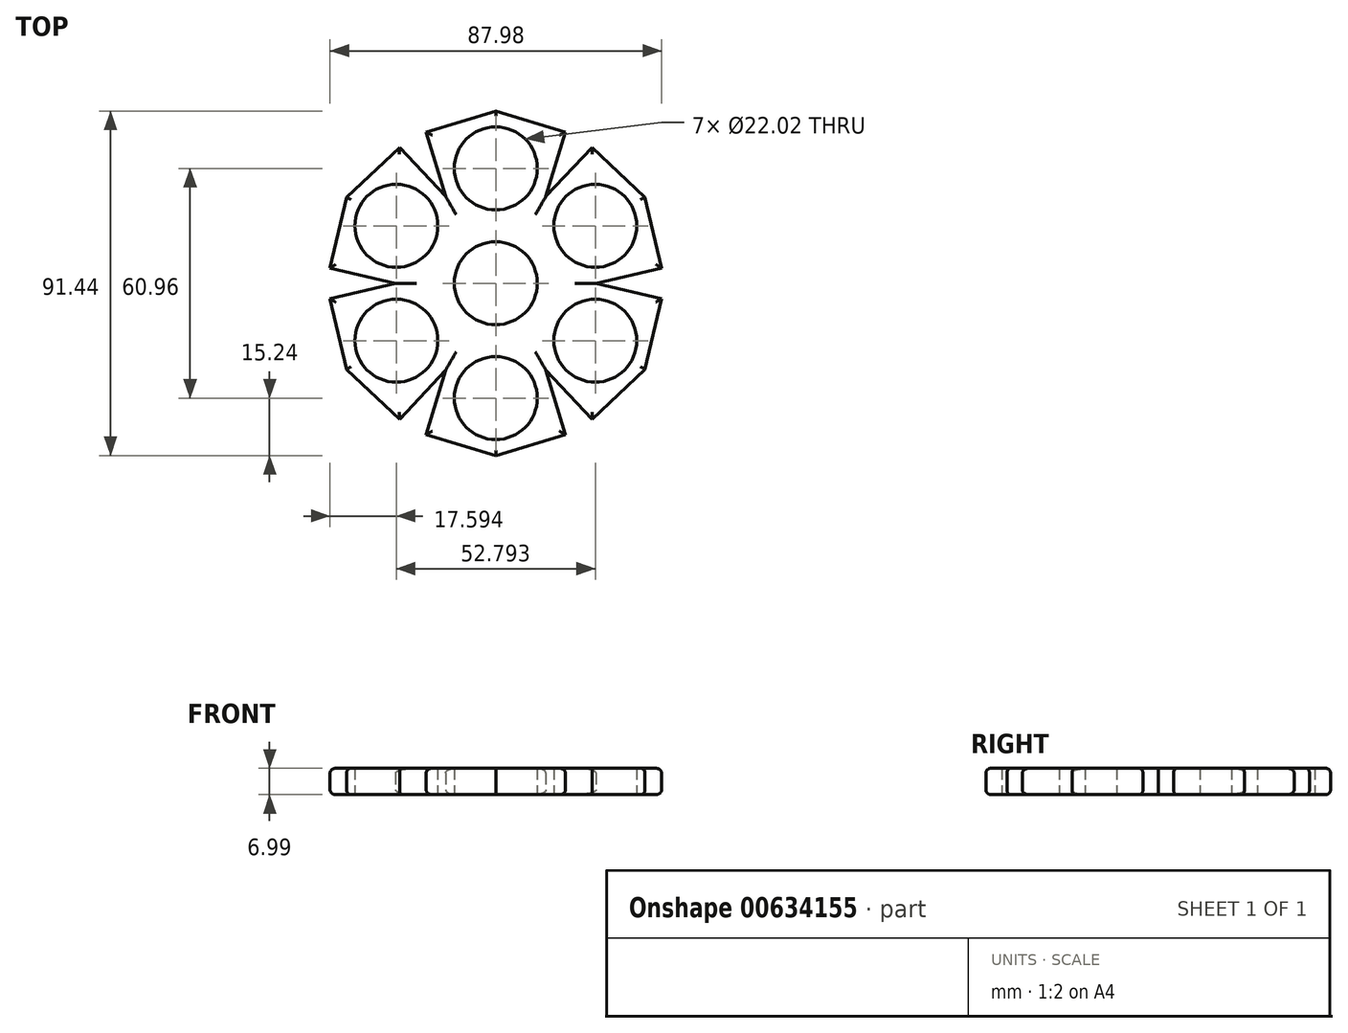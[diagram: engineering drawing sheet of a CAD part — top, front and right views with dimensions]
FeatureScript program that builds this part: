
annotation { "Feature Type Name" : "Feature", "Feature Type Description" : "" }
export const myFeature = defineFeature(function(context is Context, id is Id, definition is map)
    precondition{}
    {
        {
            var Q0;
            Q0=qCreatedBy(makeId("Top.planeOp"),FACE);
            var sketch = newSketch(context, id + "F0", { "sketchPlane" : qUnion([Q0])});
            skCircle(sketch, "E0", {"center": v(0, 0) * mm, "radius": 11.01 * mm});
            skLineSegment(sketch, "E1", {"start": v(0, 0) * mm, "end": v(0, 30.48) * mm});
            skCircle(sketch, "E2", {"center": v(0, 30.48) * mm, "radius": 11.01 * mm});
            skCircle(sketch, "E3", {"center": v(0, 0) * mm, "radius": 14.23 * mm});
            skLineSegment(sketch, "E4", {"start": v(-9.52, 10.57) * mm, "end": v(-18.48, 40.12) * mm});
            skLineSegment(sketch, "E5", {"start": v(-18.48, 40.12) * mm, "end": v(0, 45.72) * mm});
            skLineSegment(sketch, "E6", {"start": v(0, 45.72) * mm, "end": v(18.48, 40.12) * mm});
            skLineSegment(sketch, "E7", {"start": v(18.48, 40.12) * mm, "end": v(9.52, 10.57) * mm});
            skLineSegment(sketch, "E8", {"start": v(0, 45.72) * mm, "end": v(0, 0) * mm});
            skLineSegment(sketch, "E9.1.0", {"start": v(-39.6, 22.86) * mm, "end": v(0, 0) * mm});
            skCircle(sketch, "E9.1.1", {"center": v(-26.4, 15.24) * mm, "radius": 11.01 * mm});
            skLineSegment(sketch, "E9.1.2", {"start": v(-25.51, 36.06) * mm, "end": v(-4.4, 13.53) * mm});
            skLineSegment(sketch, "E9.1.3", {"start": v(-39.6, 22.86) * mm, "end": v(-25.51, 36.06) * mm});
            skLineSegment(sketch, "E9.1.4", {"start": v(-43.99, 4.06) * mm, "end": v(-39.6, 22.86) * mm});
            skLineSegment(sketch, "E9.1.5", {"start": v(-13.92, -2.96) * mm, "end": v(-43.99, 4.06) * mm});
            skLineSegment(sketch, "E9.2.0", {"start": v(-39.6, -22.86) * mm, "end": v(0, 0) * mm});
            skCircle(sketch, "E9.2.1", {"center": v(-26.4, -15.24) * mm, "radius": 11.01 * mm});
            skLineSegment(sketch, "E9.2.2", {"start": v(-43.99, -4.06) * mm, "end": v(-13.92, 2.96) * mm});
            skLineSegment(sketch, "E9.2.3", {"start": v(-39.6, -22.86) * mm, "end": v(-43.99, -4.06) * mm});
            skLineSegment(sketch, "E9.2.4", {"start": v(-25.51, -36.06) * mm, "end": v(-39.6, -22.86) * mm});
            skLineSegment(sketch, "E9.2.5", {"start": v(-4.4, -13.53) * mm, "end": v(-25.51, -36.06) * mm});
            skLineSegment(sketch, "E9.3.0", {"start": v(0, -45.72) * mm, "end": v(0, 0) * mm});
            skCircle(sketch, "E9.3.1", {"center": v(0, -30.48) * mm, "radius": 11.01 * mm});
            skLineSegment(sketch, "E9.3.2", {"start": v(-18.48, -40.12) * mm, "end": v(-9.53, -10.57) * mm});
            skLineSegment(sketch, "E9.3.3", {"start": v(0, -45.72) * mm, "end": v(-18.48, -40.12) * mm});
            skLineSegment(sketch, "E9.3.4", {"start": v(18.48, -40.12) * mm, "end": v(0, -45.72) * mm});
            skLineSegment(sketch, "E9.3.5", {"start": v(9.52, -10.57) * mm, "end": v(18.48, -40.12) * mm});
            skLineSegment(sketch, "E9.4.0", {"start": v(39.6, -22.86) * mm, "end": v(0, 0) * mm});
            skCircle(sketch, "E9.4.1", {"center": v(26.4, -15.24) * mm, "radius": 11.01 * mm});
            skLineSegment(sketch, "E9.4.2", {"start": v(25.51, -36.06) * mm, "end": v(4.4, -13.53) * mm});
            skLineSegment(sketch, "E9.4.3", {"start": v(39.6, -22.86) * mm, "end": v(25.51, -36.06) * mm});
            skLineSegment(sketch, "E9.4.4", {"start": v(43.99, -4.06) * mm, "end": v(39.6, -22.86) * mm});
            skLineSegment(sketch, "E9.4.5", {"start": v(13.92, 2.96) * mm, "end": v(43.99, -4.06) * mm});
            skLineSegment(sketch, "E9.5.0", {"start": v(39.6, 22.86) * mm, "end": v(0, 0) * mm});
            skCircle(sketch, "E9.5.1", {"center": v(26.4, 15.24) * mm, "radius": 11.01 * mm});
            skLineSegment(sketch, "E9.5.2", {"start": v(43.99, 4.06) * mm, "end": v(13.92, -2.96) * mm});
            skLineSegment(sketch, "E9.5.3", {"start": v(39.6, 22.86) * mm, "end": v(43.99, 4.06) * mm});
            skLineSegment(sketch, "E9.5.4", {"start": v(25.51, 36.06) * mm, "end": v(39.6, 22.86) * mm});
            skLineSegment(sketch, "E9.5.5", {"start": v(4.4, 13.53) * mm, "end": v(25.51, 36.06) * mm});
            skSolve(sketch);
        }
        {
            var Q0;
            Q0 = qSketchRegion(id + "F0", true);
            var Q1;
            {var subQ3=sQuery(id+"F0.wireOp",EDGE,"E9.1.0");var subQ7=sQuery(id+"F0.wireOp",EDGE,"E0");var subQ8=makeQuery(id+"F0.imprint","INTERSECT",VERTEX,{"derivedFrom":[subQ7,subQ3]});Q1=makeQuery(id+"F0.imprint","IMPRINT",FACE,{"disambiguationData":[TD([[makeQuery(id+"F0.imprint","IMPRINT",EDGE,{"disambiguationData":[TD([[subQ8,-1.0]])],"derivedFrom":subQ7}),-1.0]])]});}
            var Q2;
            {var subQ4=sQuery(id+"F0.wireOp",EDGE,"E8");var subQ5=sQuery(id+"F0.wireOp",EDGE,"E0");var subQ6=makeQuery(id+"F0.imprint","INTERSECT",VERTEX,{"derivedFrom":[subQ5,subQ4]});Q2=makeQuery(id+"F0.imprint","IMPRINT",FACE,{"disambiguationData":[TD([[makeQuery(id+"F0.imprint","IMPRINT",EDGE,{"disambiguationData":[TD([[subQ6,-1.0]])],"derivedFrom":subQ5}),-1.0]])]});}
            var Q3;
            {var subQ2=sQuery(id+"F0.wireOp",EDGE,"E8");var subQ4=sQuery(id+"F0.wireOp",EDGE,"E0");var subQ5=makeQuery(id+"F0.imprint","INTERSECT",VERTEX,{"derivedFrom":[subQ4,subQ2]});Q3=makeQuery(id+"F0.imprint","IMPRINT",FACE,{"disambiguationData":[TD([[makeQuery(id+"F0.imprint","IMPRINT",EDGE,{"disambiguationData":[TD([[subQ5,1.0]])],"derivedFrom":subQ4}),-1.0]])]});}
            var Q4;
            {var subQ5=sQuery(id+"F0.wireOp",EDGE,"E9.5.0");var subQ7=sQuery(id+"F0.wireOp",EDGE,"E0");var subQ9=makeQuery(id+"F0.imprint","INTERSECT",VERTEX,{"derivedFrom":[subQ7,subQ5]});Q4=makeQuery(id+"F0.imprint","IMPRINT",FACE,{"disambiguationData":[TD([[makeQuery(id+"F0.imprint","IMPRINT",EDGE,{"disambiguationData":[TD([[subQ9,1.0]])],"derivedFrom":subQ7}),-1.0]])]});}
            var Q5;
            {var subQ4=sQuery(id+"F0.wireOp",EDGE,"E9.3.0");var subQ5=sQuery(id+"F0.wireOp",EDGE,"E0");var subQ6=makeQuery(id+"F0.imprint","INTERSECT",VERTEX,{"derivedFrom":[subQ5,subQ4]});Q5=makeQuery(id+"F0.imprint","IMPRINT",FACE,{"disambiguationData":[TD([[makeQuery(id+"F0.imprint","IMPRINT",EDGE,{"disambiguationData":[TD([[subQ6,-1.0]])],"derivedFrom":subQ5}),-1.0]])]});}
            var Q6;
            {var subQ5=sQuery(id+"F0.wireOp",EDGE,"E9.2.0");var subQ7=sQuery(id+"F0.wireOp",EDGE,"E0");var subQ8=makeQuery(id+"F0.imprint","INTERSECT",VERTEX,{"derivedFrom":[subQ7,subQ5]});Q6=makeQuery(id+"F0.imprint","IMPRINT",FACE,{"disambiguationData":[TD([[makeQuery(id+"F0.imprint","IMPRINT",EDGE,{"disambiguationData":[TD([[subQ8,-1.0]])],"derivedFrom":subQ7}),-1.0]])]});}
            extrude(context, id + "F1", {"entities" : qUnion([Q0, Q1, Q2, Q3, Q4, Q5, Q6]), "depth" : 7 * mm, "offsetDistance" : 25.4 * mm});
        }
        {
            var Q0;
            Q0=makeQuery(id+"F1.opExtrude","CAP_EDGE",EDGE,{"disambiguationData":[OSD([sQuery(id+"F0.wireOp",EDGE,"E6")])],"isStart":false});
            var Q1;
            Q1=makeQuery(id+"F1.opExtrude","CAP_EDGE",EDGE,{"disambiguationData":[OSD([sQuery(id+"F0.wireOp",EDGE,"E7")])],"isStart":false});
            var Q2;
            Q2=makeQuery(id+"F1.opExtrude","CAP_EDGE",EDGE,{"disambiguationData":[OSD([sQuery(id+"F0.wireOp",EDGE,"E9.5.5")])],"isStart":false});
            var Q3;
            Q3=makeQuery(id+"F1.opExtrude","CAP_EDGE",EDGE,{"disambiguationData":[OSD([sQuery(id+"F0.wireOp",EDGE,"E9.5.4")])],"isStart":false});
            var Q4;
            Q4=makeQuery(id+"F1.opExtrude","CAP_EDGE",EDGE,{"disambiguationData":[OSD([sQuery(id+"F0.wireOp",EDGE,"E9.5.3")])],"isStart":false});
            var Q5;
            Q5=makeQuery(id+"F1.opExtrude","CAP_EDGE",EDGE,{"disambiguationData":[OSD([sQuery(id+"F0.wireOp",EDGE,"E9.5.2")])],"isStart":false});
            var Q6;
            Q6=makeQuery(id+"F1.opExtrude","CAP_EDGE",EDGE,{"disambiguationData":[OSD([sQuery(id+"F0.wireOp",EDGE,"E9.4.5")])],"isStart":false});
            var Q7;
            Q7=makeQuery(id+"F1.opExtrude","CAP_EDGE",EDGE,{"disambiguationData":[OSD([sQuery(id+"F0.wireOp",EDGE,"E9.4.2")])],"isStart":false});
            var Q8;
            Q8=makeQuery(id+"F1.opExtrude","CAP_EDGE",EDGE,{"disambiguationData":[OSD([sQuery(id+"F0.wireOp",EDGE,"E9.3.5")])],"isStart":false});
            var Q9;
            Q9=makeQuery(id+"F1.opExtrude","CAP_EDGE",EDGE,{"disambiguationData":[OSD([sQuery(id+"F0.wireOp",EDGE,"E9.3.2")])],"isStart":false});
            var Q10;
            Q10=makeQuery(id+"F1.opExtrude","CAP_EDGE",EDGE,{"disambiguationData":[OSD([sQuery(id+"F0.wireOp",EDGE,"E9.2.5")])],"isStart":false});
            var Q11;
            Q11=makeQuery(id+"F1.opExtrude","CAP_EDGE",EDGE,{"disambiguationData":[OSD([sQuery(id+"F0.wireOp",EDGE,"E9.2.2")])],"isStart":false});
            var Q12;
            Q12=makeQuery(id+"F1.opExtrude","CAP_EDGE",EDGE,{"disambiguationData":[OSD([sQuery(id+"F0.wireOp",EDGE,"E9.1.5")])],"isStart":false});
            var Q13;
            Q13=makeQuery(id+"F1.opExtrude","CAP_EDGE",EDGE,{"disambiguationData":[OSD([sQuery(id+"F0.wireOp",EDGE,"E9.1.2")])],"isStart":false});
            var Q14;
            Q14=makeQuery(id+"F1.opExtrude","CAP_EDGE",EDGE,{"disambiguationData":[OSD([sQuery(id+"F0.wireOp",EDGE,"E4")])],"isStart":false});
            var Q15;
            Q15=makeQuery(id+"F1.opExtrude","CAP_EDGE",EDGE,{"disambiguationData":[OSD([sQuery(id+"F0.wireOp",EDGE,"E5")])],"isStart":false});
            var Q16;
            Q16=makeQuery(id+"F1.opExtrude","CAP_EDGE",EDGE,{"disambiguationData":[OSD([sQuery(id+"F0.wireOp",EDGE,"E9.1.3")])],"isStart":false});
            var Q17;
            Q17=makeQuery(id+"F1.opExtrude","CAP_EDGE",EDGE,{"disambiguationData":[OSD([sQuery(id+"F0.wireOp",EDGE,"E9.1.4")])],"isStart":false});
            var Q18;
            Q18=makeQuery(id+"F1.opExtrude","CAP_EDGE",EDGE,{"disambiguationData":[OSD([sQuery(id+"F0.wireOp",EDGE,"E9.2.3")])],"isStart":false});
            var Q19;
            Q19=makeQuery(id+"F1.opExtrude","CAP_EDGE",EDGE,{"disambiguationData":[OSD([sQuery(id+"F0.wireOp",EDGE,"E9.2.4")])],"isStart":false});
            var Q20;
            Q20=makeQuery(id+"F1.opExtrude","CAP_EDGE",EDGE,{"disambiguationData":[OSD([sQuery(id+"F0.wireOp",EDGE,"E9.3.3")])],"isStart":false});
            var Q21;
            Q21=makeQuery(id+"F1.opExtrude","CAP_EDGE",EDGE,{"disambiguationData":[OSD([sQuery(id+"F0.wireOp",EDGE,"E9.3.4")])],"isStart":false});
            var Q22;
            Q22=makeQuery(id+"F1.opExtrude","CAP_EDGE",EDGE,{"disambiguationData":[OSD([sQuery(id+"F0.wireOp",EDGE,"E9.4.3")])],"isStart":false});
            var Q23;
            Q23=makeQuery(id+"F1.opExtrude","CAP_EDGE",EDGE,{"disambiguationData":[OSD([sQuery(id+"F0.wireOp",EDGE,"E9.4.4")])],"isStart":false});
            fillet(context, id + "F2", {"entities" : qUnion([Q0, Q1, Q2, Q3, Q4, Q5, Q6, Q7, Q8, Q9, Q10, Q11, Q12, Q13, Q14, Q15, Q16, Q17, Q18, Q19, Q20, Q21, Q22, Q23]), "radius" : 1.27 * mm, "tangentPropagation" : true, "allowEdgeOverflow" : false});
        }
        {
            var Q0;
            Q0=makeQuery(id+"F1.opExtrude","CAP_EDGE",EDGE,{"disambiguationData":[OSD([sQuery(id+"F0.wireOp",EDGE,"E9.2.4")])],"isStart":true});
            var Q1;
            Q1=makeQuery(id+"F1.opExtrude","CAP_EDGE",EDGE,{"disambiguationData":[OSD([sQuery(id+"F0.wireOp",EDGE,"E9.2.3")])],"isStart":true});
            var Q2;
            Q2=makeQuery(id+"F1.opExtrude","CAP_EDGE",EDGE,{"disambiguationData":[OSD([sQuery(id+"F0.wireOp",EDGE,"E9.2.2")])],"isStart":true});
            var Q3;
            Q3=makeQuery(id+"F1.opExtrude","CAP_EDGE",EDGE,{"disambiguationData":[OSD([sQuery(id+"F0.wireOp",EDGE,"E9.1.5")])],"isStart":true});
            var Q4;
            Q4=makeQuery(id+"F1.opExtrude","CAP_EDGE",EDGE,{"disambiguationData":[OSD([sQuery(id+"F0.wireOp",EDGE,"E9.1.4")])],"isStart":true});
            var Q5;
            Q5=makeQuery(id+"F1.opExtrude","CAP_EDGE",EDGE,{"disambiguationData":[OSD([sQuery(id+"F0.wireOp",EDGE,"E9.1.3")])],"isStart":true});
            var Q6;
            Q6=makeQuery(id+"F1.opExtrude","CAP_EDGE",EDGE,{"disambiguationData":[OSD([sQuery(id+"F0.wireOp",EDGE,"E9.1.2")])],"isStart":true});
            var Q7;
            Q7=makeQuery(id+"F1.opExtrude","CAP_EDGE",EDGE,{"disambiguationData":[OSD([sQuery(id+"F0.wireOp",EDGE,"E4")])],"isStart":true});
            var Q8;
            Q8=makeQuery(id+"F1.opExtrude","CAP_EDGE",EDGE,{"disambiguationData":[OSD([sQuery(id+"F0.wireOp",EDGE,"E7")])],"isStart":true});
            var Q9;
            Q9=makeQuery(id+"F1.opExtrude","CAP_EDGE",EDGE,{"disambiguationData":[OSD([sQuery(id+"F0.wireOp",EDGE,"E6")])],"isStart":true});
            var Q10;
            Q10=makeQuery(id+"F1.opExtrude","CAP_EDGE",EDGE,{"disambiguationData":[OSD([sQuery(id+"F0.wireOp",EDGE,"E5")])],"isStart":true});
            var Q11;
            Q11=makeQuery(id+"F1.opExtrude","CAP_EDGE",EDGE,{"disambiguationData":[OSD([sQuery(id+"F0.wireOp",EDGE,"E9.5.5")])],"isStart":true});
            var Q12;
            Q12=makeQuery(id+"F1.opExtrude","CAP_EDGE",EDGE,{"disambiguationData":[OSD([sQuery(id+"F0.wireOp",EDGE,"E9.5.4")])],"isStart":true});
            var Q13;
            Q13=makeQuery(id+"F1.opExtrude","CAP_EDGE",EDGE,{"disambiguationData":[OSD([sQuery(id+"F0.wireOp",EDGE,"E9.5.3")])],"isStart":true});
            var Q14;
            Q14=makeQuery(id+"F1.opExtrude","CAP_EDGE",EDGE,{"disambiguationData":[OSD([sQuery(id+"F0.wireOp",EDGE,"E9.4.5")])],"isStart":true});
            var Q15;
            Q15=makeQuery(id+"F1.opExtrude","CAP_EDGE",EDGE,{"disambiguationData":[OSD([sQuery(id+"F0.wireOp",EDGE,"E9.5.2")])],"isStart":true});
            var Q16;
            Q16=makeQuery(id+"F1.opExtrude","CAP_EDGE",EDGE,{"disambiguationData":[OSD([sQuery(id+"F0.wireOp",EDGE,"E9.4.4")])],"isStart":true});
            var Q17;
            Q17=makeQuery(id+"F1.opExtrude","CAP_EDGE",EDGE,{"disambiguationData":[OSD([sQuery(id+"F0.wireOp",EDGE,"E9.4.3")])],"isStart":true});
            var Q18;
            Q18=makeQuery(id+"F1.opExtrude","CAP_EDGE",EDGE,{"disambiguationData":[OSD([sQuery(id+"F0.wireOp",EDGE,"E9.3.4")])],"isStart":true});
            var Q19;
            Q19=makeQuery(id+"F1.opExtrude","CAP_EDGE",EDGE,{"disambiguationData":[OSD([sQuery(id+"F0.wireOp",EDGE,"E9.3.3")])],"isStart":true});
            var Q20;
            Q20=makeQuery(id+"F1.opExtrude","CAP_EDGE",EDGE,{"disambiguationData":[OSD([sQuery(id+"F0.wireOp",EDGE,"E9.3.2")])],"isStart":true});
            var Q21;
            Q21=makeQuery(id+"F1.opExtrude","CAP_EDGE",EDGE,{"disambiguationData":[OSD([sQuery(id+"F0.wireOp",EDGE,"E9.2.5")])],"isStart":true});
            var Q22;
            Q22=makeQuery(id+"F1.opExtrude","CAP_EDGE",EDGE,{"disambiguationData":[OSD([sQuery(id+"F0.wireOp",EDGE,"E9.3.5")])],"isStart":true});
            var Q23;
            Q23=makeQuery(id+"F1.opExtrude","CAP_EDGE",EDGE,{"disambiguationData":[OSD([sQuery(id+"F0.wireOp",EDGE,"E9.4.2")])],"isStart":true});
            fillet(context, id + "F3", {"entities" : qUnion([Q0, Q1, Q2, Q3, Q4, Q5, Q6, Q7, Q8, Q9, Q10, Q11, Q12, Q13, Q14, Q15, Q16, Q17, Q18, Q19, Q20, Q21, Q22, Q23]), "radius" : 1.27 * mm, "tangentPropagation" : true, "allowEdgeOverflow" : false});
        }
    });
